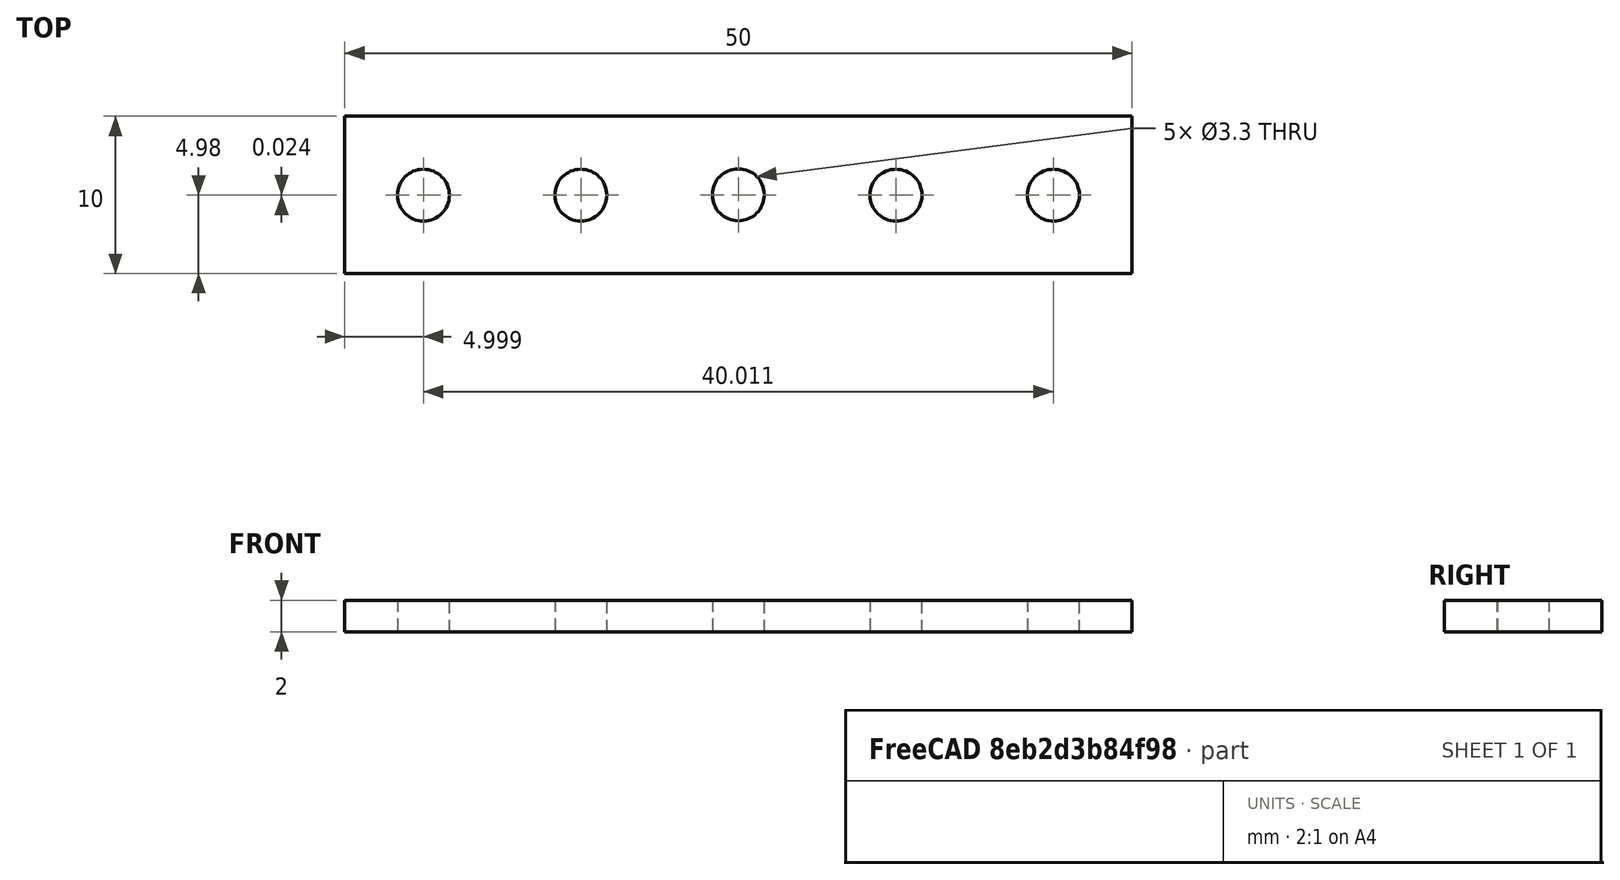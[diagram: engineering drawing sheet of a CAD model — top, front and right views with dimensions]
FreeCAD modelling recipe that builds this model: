
FCSTD DOCUMENT  (FreeCAD 1.0R38806 (Git))
Label: pieza_mecano
License: All rights reserved
LicenseURL: https://en.wikipedia.org/wiki/All_rights_reserved
objects: Sketcher::SketchObject×1, Part::Extrusion×1
note: 3 computed .brp shape members not serialized (recipe doc carries the construction recipe); baked Part::Feature solids carry a one-line shape summary decoded from their .brp

FEATURE [Sketcher::SketchObject] Sketch
  ArcFitTolerance = 1e-06
  FullyConstrained = false
  MakeInternals = false
  sketch-geometry (10):
    g0: LineSegment StartX=-25.0112 StartY=5.02361 StartZ=0 EndX=-25.0112 EndY=-4.97639 EndZ=0
    g1: LineSegment StartX=-25.0112 StartY=-4.97639 StartZ=0 EndX=24.9888 EndY=-4.97639 EndZ=0
    g2: LineSegment StartX=24.9888 StartY=-4.97639 StartZ=0 EndX=24.9888 EndY=5.02361 EndZ=0
    g3: LineSegment StartX=24.9888 StartY=5.02361 StartZ=0 EndX=-25.0112 EndY=5.02361 EndZ=0
    g4: GeomPoint [constr] X=-0.0112475 Y=0.023613 Z=0
    g5: Circle CenterX=-0.0112475 CenterY=0.023613 CenterZ=0 NormalX=0 NormalY=0 NormalZ=1 AngleXU=0 Radius=1.65
    g6: Circle CenterX=-10.0112 CenterY=0 CenterZ=0 NormalX=0 NormalY=0 NormalZ=1 AngleXU=0 Radius=1.65
    g7: Circle CenterX=-20.0112 CenterY=0 CenterZ=0 NormalX=0 NormalY=0 NormalZ=1 AngleXU=0 Radius=1.65
    g8: Circle CenterX=10 CenterY=0 CenterZ=0 NormalX=0 NormalY=0 NormalZ=1 AngleXU=0 Radius=1.65
    g9: Circle CenterX=20 CenterY=0 CenterZ=0 NormalX=0 NormalY=0 NormalZ=1 AngleXU=0 Radius=1.65
  constraints (19):
    c: Coincident(g0,g1)
    c: Coincident(g1,g2)
    c: Coincident(g2,g3)
    c: Coincident(g3,g0)
    c: Vertical(g0)
    c: Vertical(g2)
    c: Horizontal(g1)
    c: Horizontal(g3)
    c: Symmetric(g2,g0,g4)
    c: Coincident(g5,g4)
    c: DistanceX(g1,g1) = 50
    c: Distance(g2,g2) = 10
    c: Diameter(g5) = 3.3
    c: PointOnObject(g6,g-1)
    c: DistanceX(g6,g4) = 10
    c: PointOnObject(g7,g-1)
    c: DistanceX(g7,g6) = 10
    c: PointOnObject(g8,g-1)
    c: PointOnObject(g9,g-1)
FEATURE [Part::Extrusion] Extrude
  Base = -> Sketch
  Dir = (0,0,1)
  DirMode = 0
  FaceMakerClass = Part::FaceMakerBullseye
  FaceMakerMode = 3
  LengthFwd = 2
  LengthRev = 0
  Solid = true
  Symmetric = false
